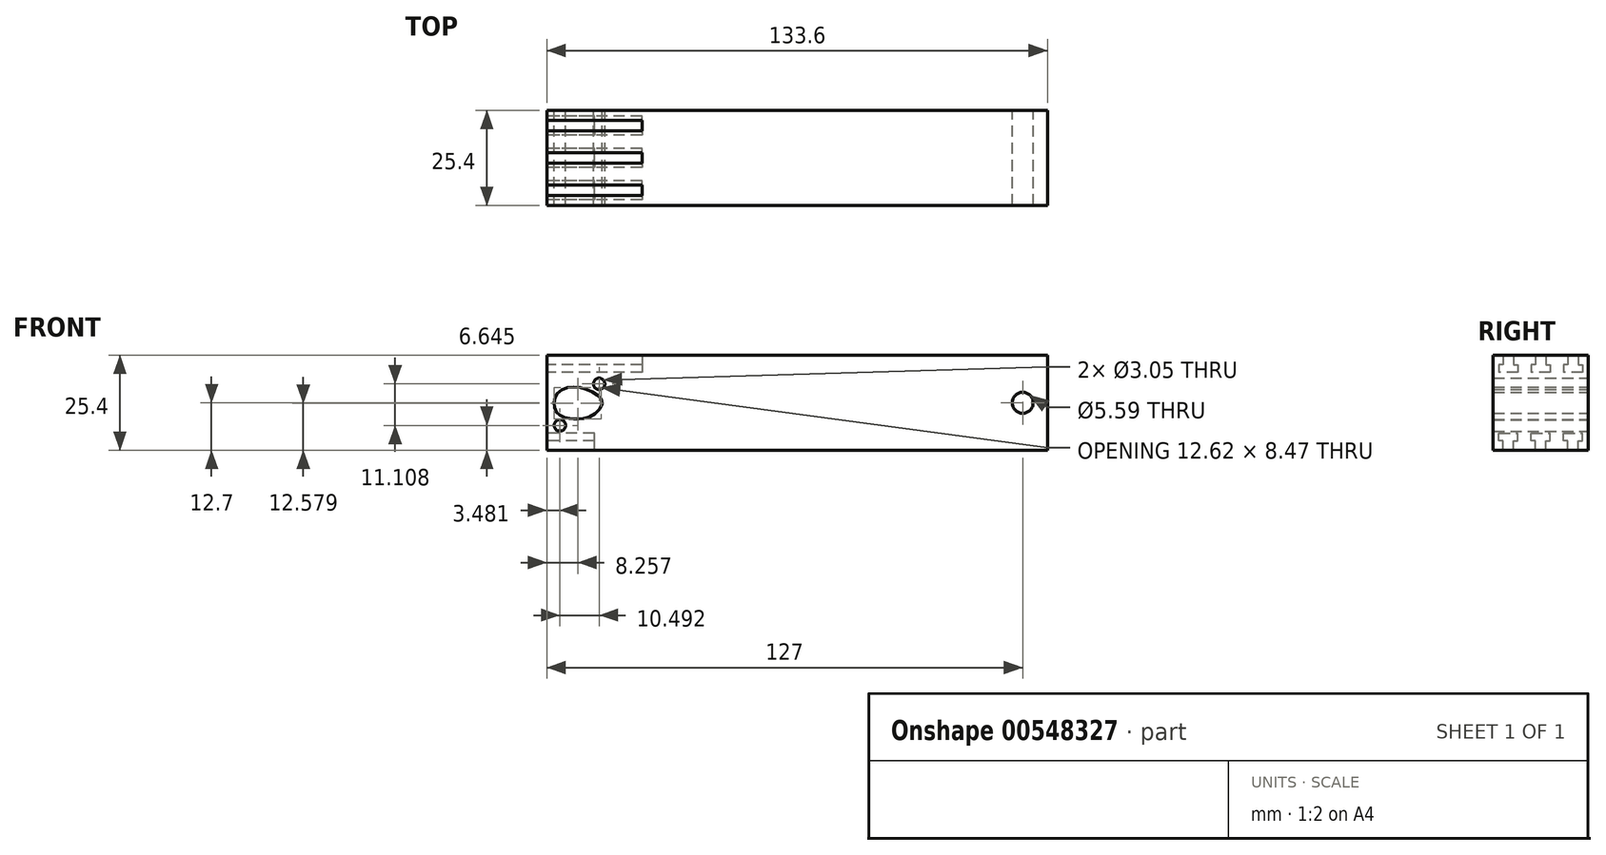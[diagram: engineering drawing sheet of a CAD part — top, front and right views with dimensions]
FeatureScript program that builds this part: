
annotation { "Feature Type Name" : "Feature", "Feature Type Description" : "" }
export const myFeature = defineFeature(function(context is Context, id is Id, definition is map)
    precondition{}
    {
        {
            var Q0;
            Q0=qCreatedBy(makeId("Front.planeOp"),FACE);
            var sketch = newSketch(context, id + "F0", { "sketchPlane" : qUnion([Q0])});
            skLineSegment(sketch, "E0", {"start": v(0, 12.7) * mm, "end": v(6.6, 12.7) * mm});
            skLineSegment(sketch, "E1", {"start": v(-127, 12.7) * mm, "end": v(0, 12.7) * mm});
            skCircle(sketch, "E2", {"center": v(0, 0) * mm, "radius": 2.8 * mm});
            skLineSegment(sketch, "E3", {"start": v(-127, 12.7) * mm, "end": v(-127, 0) * mm});
            skLineSegment(sketch, "E4", {"start": v(6.6, 12.7) * mm, "end": v(6.6, 0) * mm});
            skLineSegment(sketch, "E5.MirrorCS", {"start": v(6.6, -12.7) * mm, "end": v(6.6, 0) * mm});
            skLineSegment(sketch, "E6.MirrorCS", {"start": v(0, -12.7) * mm, "end": v(6.6, -12.7) * mm});
            skLineSegment(sketch, "E7.MirrorCS", {"start": v(-127, -12.7) * mm, "end": v(0, -12.7) * mm});
            skLineSegment(sketch, "E8.MirrorCS", {"start": v(-127, -12.7) * mm, "end": v(-127, 0) * mm});
            skFitSpline(sketch, "E9", {"points": [v(-125.05, 0) * mm, v(-123.82, 3) * mm, v(-119.35, 4.18) * mm, v(-114.5, 2.74) * mm, v(-112.17, 0) * mm, v(-115.08, -3.51) * mm, v(-118.83, -4.38) * mm, v(-121.41, -4.14) * mm, v(-124.28, -2.7) * mm, v(-125.05, 0) * mm]});
            skCircle(sketch, "E10", {"center": v(-123.52, -6.05) * mm, "radius": 1.52 * mm});
            skCircle(sketch, "E11", {"center": v(-113.03, 5.05) * mm, "radius": 1.52 * mm});
            skPoint(sketch, "E12.orphan", {"position": v(-127, -12.7) * mm});
            skSolve(sketch);
        }
        {
            var Q0;
            Q0=makeQuery(id+"F0.imprint","IMPRINT",FACE,{"disambiguationData":[TD([[makeQuery(id+"F0.imprint","IMPRINT",EDGE,{"derivedFrom":sQuery(id+"F0.wireOp",EDGE,"E0")}),-1.0]])]});
            extrude(context, id + "F1", {"entities" : qUnion([Q0]), "endBound" : BoundingType.SYMMETRIC, "depth" : 25.4 * mm, "offsetDistance" : 25.4 * mm});
        }
        {
            var Q0;
            Q0=makeQuery(id+"F0.imprint","IMPRINT",FACE,{"disambiguationData":[TD([[makeQuery(id+"F0.imprint","IMPRINT",EDGE,{"derivedFrom":sQuery(id+"F0.wireOp",EDGE,"E9")}),-1.0]])]});
            extrude(context, id + "F2", {"entities" : qUnion([Q0]), "operationType" : NewBodyOperationType.REMOVE, "endBound" : BoundingType.THROUGH_ALL, "oppositeDirection" : true, "depth" : 25.4 * mm, "offsetDistance" : 25.4 * mm});
        }
        {
            var Q0;
            Q0=makeQuery(id+"F1.opExtrude","SWEPT_FACE",FACE,{"disambiguationData":[OSD([sQuery(id+"F0.wireOp",EDGE,"E3"),sQuery(id+"F0.wireOp",EDGE,"E8.MirrorCS")])]});
            var sketch = newSketch(context, id + "F3", { "sketchPlane" : qUnion([Q0])});
            skLineSegment(sketch, "E13", {"start": v(-1.4, -12.7) * mm, "end": v(-1.4, -10.16) * mm});
            skLineSegment(sketch, "E14", {"start": v(-1.4, -10.16) * mm, "end": v(-2.54, -10.16) * mm});
            skLineSegment(sketch, "E15", {"start": v(-2.54, -10.16) * mm, "end": v(-2.54, -8.13) * mm});
            skLineSegment(sketch, "E16", {"start": v(-2.54, -8.13) * mm, "end": v(0, -8.13) * mm});
            skLineSegment(sketch, "E17", {"start": v(-1.4, -12.7) * mm, "end": v(0, -12.7) * mm});
            skLineSegment(sketch, "E18.MirrorCS", {"start": v(2.54, -8.13) * mm, "end": v(0, -8.13) * mm});
            skLineSegment(sketch, "E19.MirrorCS", {"start": v(2.54, -10.16) * mm, "end": v(2.54, -8.13) * mm});
            skLineSegment(sketch, "E20.MirrorCS", {"start": v(1.4, -10.16) * mm, "end": v(2.54, -10.16) * mm});
            skLineSegment(sketch, "E21.MirrorCS", {"start": v(1.4, -12.7) * mm, "end": v(1.4, -10.16) * mm});
            skLineSegment(sketch, "E22.MirrorCS", {"start": v(1.4, -12.7) * mm, "end": v(0, -12.7) * mm});
            skLineSegment(sketch, "E23", {"start": v(-4.32, -12.7) * mm, "end": v(-4.32, -5.2) * mm, "construction": true});
            skLineSegment(sketch, "E24.MirrorCS", {"start": v(-6.1, -10.16) * mm, "end": v(-6.1, -8.13) * mm});
            skLineSegment(sketch, "E25.MirrorCS", {"start": v(-7.24, -10.16) * mm, "end": v(-6.1, -10.16) * mm});
            skLineSegment(sketch, "E26.MirrorCS", {"start": v(-6.1, -8.13) * mm, "end": v(-8.64, -8.13) * mm});
            skLineSegment(sketch, "E27.MirrorCS", {"start": v(-11.18, -8.13) * mm, "end": v(-8.64, -8.13) * mm});
            skLineSegment(sketch, "E28.MirrorCS", {"start": v(-10.03, -10.16) * mm, "end": v(-11.18, -10.16) * mm});
            skLineSegment(sketch, "E29.MirrorCS", {"start": v(-11.18, -10.16) * mm, "end": v(-11.18, -8.13) * mm});
            skLineSegment(sketch, "E30.MirrorCS", {"start": v(-10.03, -12.7) * mm, "end": v(-10.03, -10.16) * mm});
            skLineSegment(sketch, "E31.MirrorCS", {"start": v(-7.24, -12.7) * mm, "end": v(-7.24, -10.16) * mm});
            skLineSegment(sketch, "E32.MirrorCS", {"start": v(-7.24, -12.7) * mm, "end": v(-8.64, -12.7) * mm});
            skLineSegment(sketch, "E33.MirrorCS", {"start": v(-10.03, -12.7) * mm, "end": v(-8.64, -12.7) * mm});
            skLineSegment(sketch, "E34.MirrorCS", {"start": v(4.32, -12.7) * mm, "end": v(4.32, -5.2) * mm, "construction": true});
            skLineSegment(sketch, "E35.MirrorCS", {"start": v(6.1, -8.13) * mm, "end": v(8.64, -8.13) * mm});
            skLineSegment(sketch, "E36.MirrorCS", {"start": v(11.18, -8.13) * mm, "end": v(8.64, -8.13) * mm});
            skLineSegment(sketch, "E37.MirrorCS", {"start": v(11.18, -10.16) * mm, "end": v(11.18, -8.13) * mm});
            skLineSegment(sketch, "E38.MirrorCS", {"start": v(10.03, -10.16) * mm, "end": v(11.18, -10.16) * mm});
            skLineSegment(sketch, "E39.MirrorCS", {"start": v(7.24, -10.16) * mm, "end": v(6.1, -10.16) * mm});
            skLineSegment(sketch, "E40.MirrorCS", {"start": v(6.1, -10.16) * mm, "end": v(6.1, -8.13) * mm});
            skLineSegment(sketch, "E41.MirrorCS", {"start": v(7.24, -12.7) * mm, "end": v(7.24, -10.16) * mm});
            skLineSegment(sketch, "E42.MirrorCS", {"start": v(10.03, -12.7) * mm, "end": v(10.03, -10.16) * mm});
            skLineSegment(sketch, "E43.MirrorCS", {"start": v(10.03, -12.7) * mm, "end": v(8.64, -12.7) * mm});
            skLineSegment(sketch, "E44.MirrorCS", {"start": v(7.24, -12.7) * mm, "end": v(8.64, -12.7) * mm});
            skLineSegment(sketch, "E45.MirrorCS", {"start": v(10.03, 12.7) * mm, "end": v(10.03, 10.16) * mm});
            skLineSegment(sketch, "E46.MirrorCS", {"start": v(-6.1, 8.13) * mm, "end": v(-8.64, 8.13) * mm});
            skLineSegment(sketch, "E47.MirrorCS", {"start": v(6.1, 10.16) * mm, "end": v(6.1, 8.13) * mm});
            skLineSegment(sketch, "E48.MirrorCS", {"start": v(7.24, 10.16) * mm, "end": v(6.1, 10.16) * mm});
            skLineSegment(sketch, "E49.MirrorCS", {"start": v(-7.24, 12.7) * mm, "end": v(-8.64, 12.7) * mm});
            skLineSegment(sketch, "E50.MirrorCS", {"start": v(-7.24, 12.7) * mm, "end": v(-7.24, 10.16) * mm});
            skLineSegment(sketch, "E51.MirrorCS", {"start": v(-10.03, 12.7) * mm, "end": v(-10.03, 10.16) * mm});
            skLineSegment(sketch, "E52.MirrorCS", {"start": v(6.1, 8.13) * mm, "end": v(8.64, 8.13) * mm});
            skLineSegment(sketch, "E53.MirrorCS", {"start": v(-6.1, 10.16) * mm, "end": v(-6.1, 8.13) * mm});
            skLineSegment(sketch, "E54.MirrorCS", {"start": v(7.24, 12.7) * mm, "end": v(7.24, 10.16) * mm});
            skLineSegment(sketch, "E55.MirrorCS", {"start": v(-1.4, 12.7) * mm, "end": v(0, 12.7) * mm});
            skLineSegment(sketch, "E56.MirrorCS", {"start": v(1.4, 12.7) * mm, "end": v(1.4, 10.16) * mm});
            skLineSegment(sketch, "E57.MirrorCS", {"start": v(2.54, 8.13) * mm, "end": v(0, 8.13) * mm});
            skLineSegment(sketch, "E58.MirrorCS", {"start": v(2.54, 10.16) * mm, "end": v(2.54, 8.13) * mm});
            skLineSegment(sketch, "E59.MirrorCS", {"start": v(1.4, 10.16) * mm, "end": v(2.54, 10.16) * mm});
            skLineSegment(sketch, "E60.MirrorCS", {"start": v(-2.54, 8.13) * mm, "end": v(0, 8.13) * mm});
            skLineSegment(sketch, "E61.MirrorCS", {"start": v(-1.4, 12.7) * mm, "end": v(-1.4, 10.16) * mm});
            skLineSegment(sketch, "E62.MirrorCS", {"start": v(-10.03, 12.7) * mm, "end": v(-8.64, 12.7) * mm});
            skLineSegment(sketch, "E63.MirrorCS", {"start": v(11.18, 8.13) * mm, "end": v(8.64, 8.13) * mm});
            skLineSegment(sketch, "E64.MirrorCS", {"start": v(11.18, 10.16) * mm, "end": v(11.18, 8.13) * mm});
            skLineSegment(sketch, "E65.MirrorCS", {"start": v(7.24, 12.7) * mm, "end": v(8.64, 12.7) * mm});
            skLineSegment(sketch, "E66.MirrorCS", {"start": v(-11.18, 10.16) * mm, "end": v(-11.18, 8.13) * mm});
            skLineSegment(sketch, "E67.MirrorCS", {"start": v(10.03, 12.7) * mm, "end": v(8.64, 12.7) * mm});
            skLineSegment(sketch, "E68.MirrorCS", {"start": v(-7.24, 10.16) * mm, "end": v(-6.1, 10.16) * mm});
            skLineSegment(sketch, "E69.MirrorCS", {"start": v(-10.03, 10.16) * mm, "end": v(-11.18, 10.16) * mm});
            skLineSegment(sketch, "E70.MirrorCS", {"start": v(-1.4, 10.16) * mm, "end": v(-2.54, 10.16) * mm});
            skLineSegment(sketch, "E71.MirrorCS", {"start": v(-11.18, 8.13) * mm, "end": v(-8.64, 8.13) * mm});
            skLineSegment(sketch, "E72.MirrorCS", {"start": v(1.4, 12.7) * mm, "end": v(0, 12.7) * mm});
            skLineSegment(sketch, "E73.MirrorCS", {"start": v(-2.54, 10.16) * mm, "end": v(-2.54, 8.13) * mm});
            skLineSegment(sketch, "E74.MirrorCS", {"start": v(10.03, 10.16) * mm, "end": v(11.18, 10.16) * mm});
            skSolve(sketch);
        }
        {
            var Q0;
            Q0=makeQuery(id+"F3.imprint","IMPRINT",FACE,{"disambiguationData":[TD([[makeQuery(id+"F3.imprint","IMPRINT",EDGE,{"derivedFrom":sQuery(id+"F3.wireOp",EDGE,"E24.MirrorCS")}),1.0]])]});
            var Q1;
            Q1=makeQuery(id+"F3.imprint","IMPRINT",FACE,{"disambiguationData":[TD([[makeQuery(id+"F3.imprint","IMPRINT",EDGE,{"derivedFrom":sQuery(id+"F3.wireOp",EDGE,"E13")}),-1.0]])]});
            var Q2;
            Q2=makeQuery(id+"F3.imprint","IMPRINT",FACE,{"disambiguationData":[TD([[makeQuery(id+"F3.imprint","IMPRINT",EDGE,{"derivedFrom":sQuery(id+"F3.wireOp",EDGE,"E35.MirrorCS")}),-1.0]])]});
            extrude(context, id + "F4", {"entities" : qUnion([Q0, Q1, Q2]), "operationType" : NewBodyOperationType.REMOVE, "oppositeDirection" : true, "depth" : 12.7 * mm, "offsetDistance" : 25.4 * mm});
        }
        {
            var Q0;
            Q0=makeQuery(id+"F3.imprint","IMPRINT",FACE,{"disambiguationData":[TD([[makeQuery(id+"F3.imprint","IMPRINT",EDGE,{"derivedFrom":sQuery(id+"F3.wireOp",EDGE,"E46.MirrorCS")}),-1.0]])]});
            var Q1;
            Q1=makeQuery(id+"F3.imprint","IMPRINT",FACE,{"disambiguationData":[TD([[makeQuery(id+"F3.imprint","IMPRINT",EDGE,{"derivedFrom":sQuery(id+"F3.wireOp",EDGE,"E55.MirrorCS")}),1.0]])]});
            var Q2;
            Q2=makeQuery(id+"F3.imprint","IMPRINT",FACE,{"disambiguationData":[TD([[makeQuery(id+"F3.imprint","IMPRINT",EDGE,{"derivedFrom":sQuery(id+"F3.wireOp",EDGE,"E45.MirrorCS")}),-1.0]])]});
            extrude(context, id + "F5", {"entities" : qUnion([Q0, Q1, Q2]), "operationType" : NewBodyOperationType.REMOVE, "oppositeDirection" : true, "depth" : 25.4 * mm, "offsetDistance" : 25.4 * mm});
        }
    });
